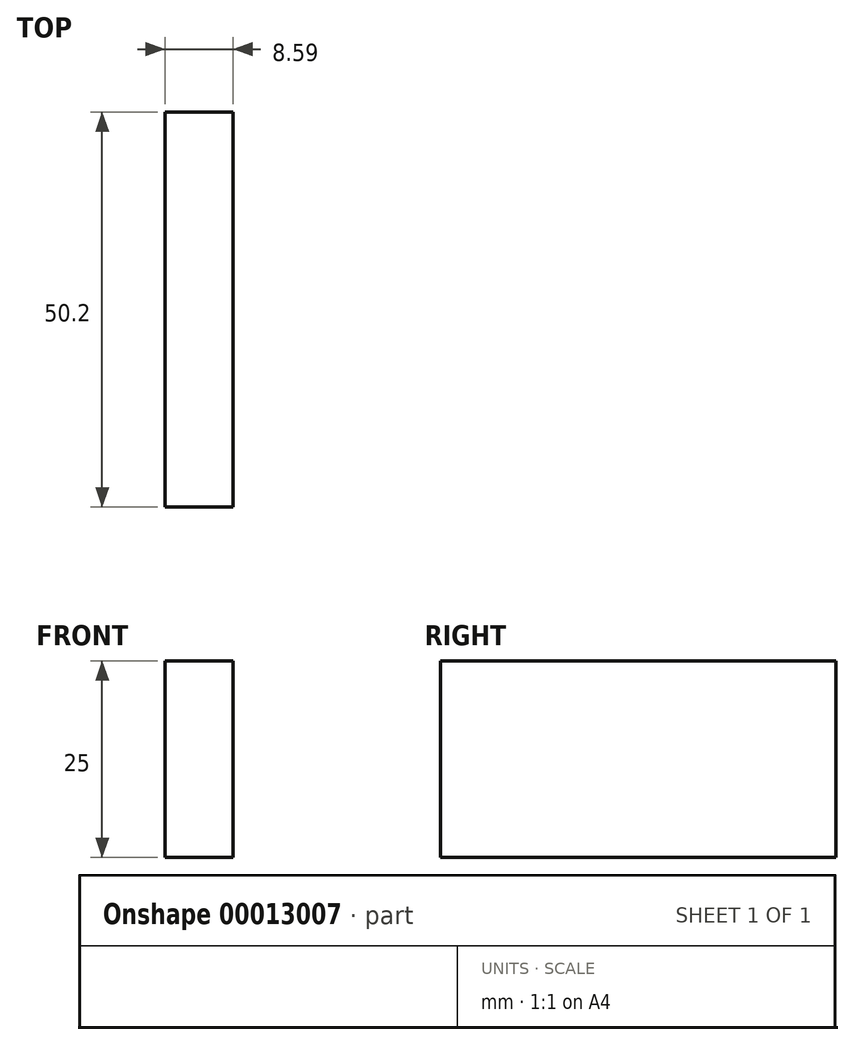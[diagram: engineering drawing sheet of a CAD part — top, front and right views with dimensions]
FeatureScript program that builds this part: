
annotation { "Feature Type Name" : "Feature", "Feature Type Description" : "" }
export const myFeature = defineFeature(function(context is Context, id is Id, definition is map)
    precondition{}
    {
        {
            var Q0;
            Q0=qCreatedBy(makeId("Top.planeOp"),FACE);
            var sketch = newSketch(context, id + "F0", { "sketchPlane" : qUnion([Q0])});
            skLineSegment(sketch, "E0.bottom", {"start": v(47.38, -28.25) * mm, "end": v(-31.27, -28.25) * mm});
            skLineSegment(sketch, "E0.top", {"start": v(47.38, 36.69) * mm, "end": v(-31.27, 36.69) * mm});
            skLineSegment(sketch, "E0.left", {"start": v(47.38, -28.25) * mm, "end": v(47.38, 36.69) * mm});
            skLineSegment(sketch, "E0.right", {"start": v(-31.27, -28.25) * mm, "end": v(-31.27, 36.69) * mm});
            skLineSegment(sketch, "E1.bottom", {"start": v(38.8, 21.95) * mm, "end": v(47.38, 21.95) * mm});
            skLineSegment(sketch, "E1.top", {"start": v(38.8, -28.25) * mm, "end": v(47.38, -28.25) * mm});
            skLineSegment(sketch, "E1.left", {"start": v(38.8, 21.95) * mm, "end": v(38.8, -28.25) * mm});
            skLineSegment(sketch, "E1.right", {"start": v(47.38, 21.95) * mm, "end": v(47.38, -28.25) * mm});
            skSolve(sketch);
        }
        {
            var Q0;
            Q0=makeQuery(id+"F0.imprint","IMPRINT",FACE,{"disambiguationData":[TD([[makeQuery(id+"F0.imprint","IMPRINT",EDGE,{"derivedFrom":sQuery(id+"F0.wireOp",EDGE,"E1.bottom")}),-1.0]])]});
            extrude(context, id + "F1", {"entities" : qUnion([Q0]), "depth" : 25 * mm});
        }
        {
            var Q0;
            Q0=makeQuery(id+"F0.imprint","IMPRINT",FACE,{"disambiguationData":[TD([[makeQuery(id+"F0.imprint","IMPRINT",EDGE,{"derivedFrom":sQuery(id+"F0.wireOp",EDGE,"E1.bottom")}),-1.0]])]});
            var Q1;
            Q1=makeQuery(id+"F0.imprint","IMPRINT",FACE,{"disambiguationData":[TD([[makeQuery(id+"F0.imprint","IMPRINT",EDGE,{"derivedFrom":sQuery(id+"F0.wireOp",EDGE,"E0.bottom")}),-1.0]])]});
            extrude(context, id + "F3", {"entities" : qUnion([Q0, Q1]), "operationType" : NewBodyOperationType.ADD, "depth" : 9 * mm});
        }
    });
